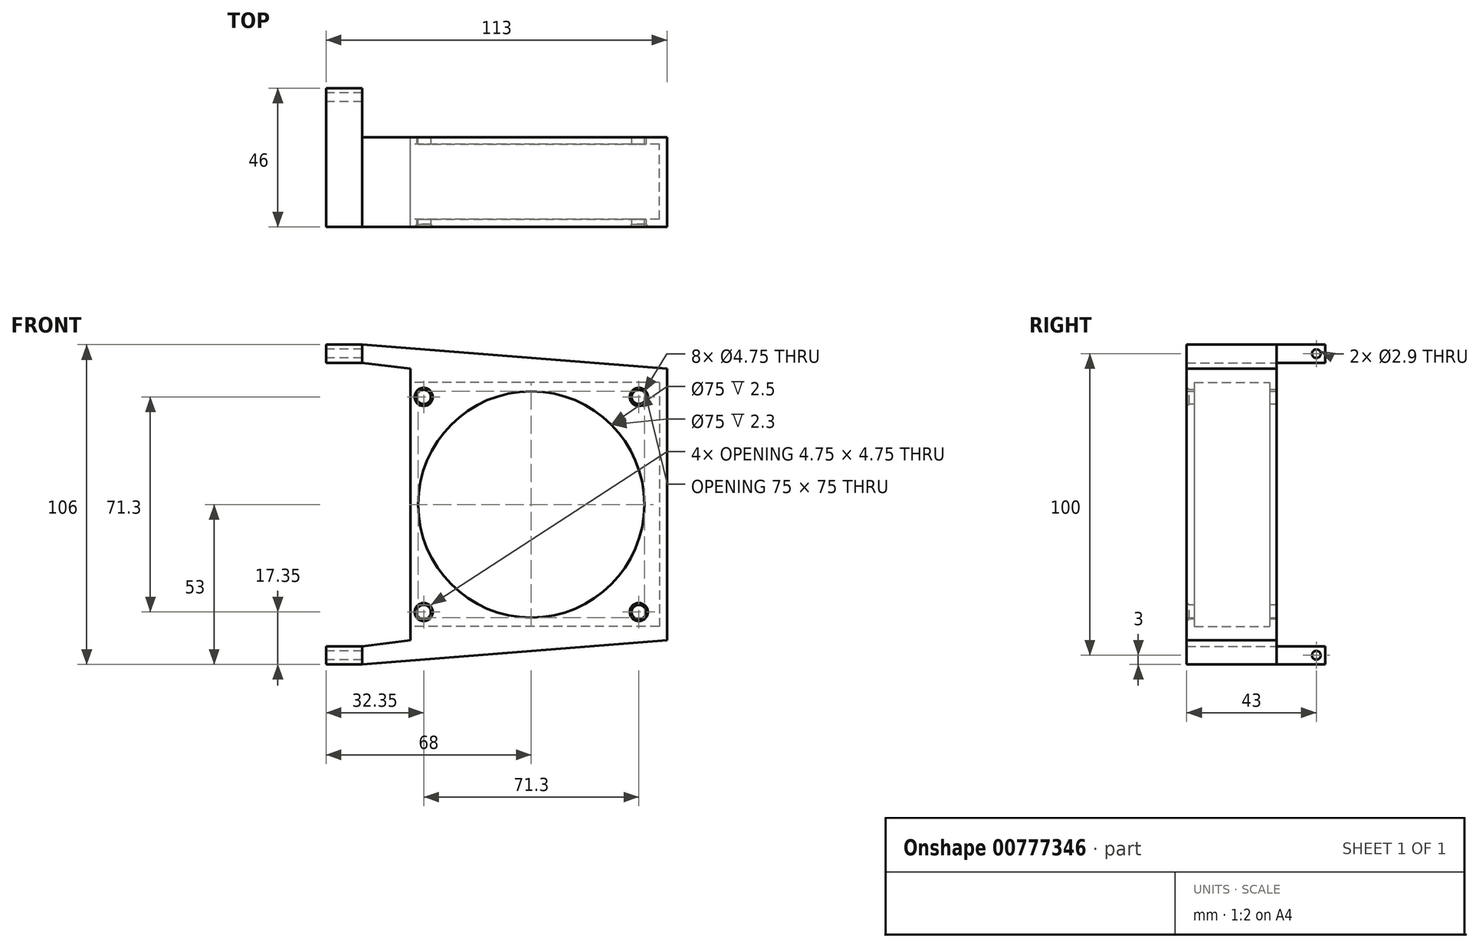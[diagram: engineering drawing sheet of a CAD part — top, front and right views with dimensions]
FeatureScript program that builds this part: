
annotation { "Feature Type Name" : "Feature", "Feature Type Description" : "" }
export const myFeature = defineFeature(function(context is Context, id is Id, definition is map)
    precondition{}
    {
        {
            var Q0;
            Q0=qCreatedBy(makeId("Front.planeOp"),FACE);
            var sketch = newSketch(context, id + "F0", { "sketchPlane" : qUnion([Q0])});
            skLineSegment(sketch, "E0.bottom", {"start": v(-35.65, 35.65) * mm, "end": v(35.65, 35.65) * mm, "construction": true});
            skLineSegment(sketch, "E0.top", {"start": v(-35.65, -35.65) * mm, "end": v(35.65, -35.65) * mm, "construction": true});
            skLineSegment(sketch, "E0.left", {"start": v(-35.65, 35.65) * mm, "end": v(-35.65, -35.65) * mm, "construction": true});
            skLineSegment(sketch, "E0.right", {"start": v(35.65, 35.65) * mm, "end": v(35.65, -35.65) * mm, "construction": true});
            skPoint(sketch, "E0.middle", {"position": v(0, 0) * mm});
            skLineSegment(sketch, "E1.bottom", {"start": v(-40, 40) * mm, "end": v(40, 40) * mm});
            skLineSegment(sketch, "E1.top", {"start": v(-40, -40) * mm, "end": v(40, -40) * mm});
            skLineSegment(sketch, "E1.left", {"start": v(-40, 40) * mm, "end": v(-40, -40) * mm});
            skLineSegment(sketch, "E1.right", {"start": v(40, 40) * mm, "end": v(40, -40) * mm});
            skPoint(sketch, "E2.middle", {"position": v(-58, 0) * mm});
            skPoint(sketch, "E2.middle.positionSnap0", {"position": v(-40, 0) * mm});
            skPoint(sketch, "E2.centerSnap0", {"position": v(-40, 0) * mm});
            skLineSegment(sketch, "E3.bottom", {"start": v(-68, 50) * mm, "end": v(-48, 50) * mm, "construction": true});
            skLineSegment(sketch, "E3.top", {"start": v(-68, -50) * mm, "end": v(-48, -50) * mm, "construction": true});
            skLineSegment(sketch, "E3.left", {"start": v(-68, 50) * mm, "end": v(-68, -50) * mm, "construction": true});
            skLineSegment(sketch, "E3.right", {"start": v(-48, 50) * mm, "end": v(-48, -50) * mm, "construction": true});
            skLineSegment(sketch, "E4.bottom", {"start": v(-56, 47) * mm, "end": v(-68, 47) * mm});
            skLineSegment(sketch, "E4.top", {"start": v(-56, 53) * mm, "end": v(-68, 53) * mm});
            skLineSegment(sketch, "E4.left", {"start": v(-56, 47) * mm, "end": v(-56, 53) * mm});
            skLineSegment(sketch, "E4.right", {"start": v(-68, 47) * mm, "end": v(-68, 53) * mm});
            skPoint(sketch, "E4.middle", {"position": v(-62, 50) * mm});
            skLineSegment(sketch, "E5.MirrorCS", {"start": v(-68, -47) * mm, "end": v(-68, -53) * mm});
            skLineSegment(sketch, "E6.MirrorCS", {"start": v(-56, -47) * mm, "end": v(-68, -47) * mm});
            skLineSegment(sketch, "E7.MirrorCS", {"start": v(-56, -53) * mm, "end": v(-68, -53) * mm});
            skLineSegment(sketch, "E8.MirrorCS", {"start": v(-56, -47) * mm, "end": v(-56, -53) * mm});
            skPoint(sketch, "E9.MirrorP", {"position": v(-62, -50) * mm});
            skLineSegment(sketch, "E10.bottom", {"start": v(-68, 47) * mm, "end": v(-56, 47) * mm});
            skLineSegment(sketch, "E10.top", {"start": v(-68, -47) * mm, "end": v(-56, -47) * mm});
            skLineSegment(sketch, "E10.left", {"start": v(-68, 47) * mm, "end": v(-68, -47) * mm});
            skLineSegment(sketch, "E10.right", {"start": v(-56, 47) * mm, "end": v(-56, -47) * mm});
            skLineSegment(sketch, "E11.bottom", {"start": v(40, 40) * mm, "end": v(45, 40) * mm, "construction": true});
            skLineSegment(sketch, "E11.top", {"start": v(40, 45) * mm, "end": v(45, 45) * mm, "construction": true});
            skLineSegment(sketch, "E11.left", {"start": v(40, 40) * mm, "end": v(40, 45) * mm, "construction": true});
            skLineSegment(sketch, "E11.right", {"start": v(45, 40) * mm, "end": v(45, 45) * mm, "construction": true});
            skLineSegment(sketch, "E12.MirrorCS", {"start": v(45, -40) * mm, "end": v(45, -45) * mm, "construction": true});
            skLineSegment(sketch, "E13.MirrorCS", {"start": v(40, -40) * mm, "end": v(45, -40) * mm, "construction": true});
            skLineSegment(sketch, "E14.MirrorCS", {"start": v(40, -45) * mm, "end": v(45, -45) * mm, "construction": true});
            skLineSegment(sketch, "E15.MirrorCS", {"start": v(40, -40) * mm, "end": v(40, -45) * mm, "construction": true});
            skLineSegment(sketch, "E16.bottom", {"start": v(45, 45) * mm, "end": v(-40, 45) * mm});
            skLineSegment(sketch, "E16.top", {"start": v(45, -45) * mm, "end": v(-40, -45) * mm});
            skLineSegment(sketch, "E16.left", {"start": v(45, 45) * mm, "end": v(45, -45) * mm});
            skLineSegment(sketch, "E16.right", {"start": v(-40, 45) * mm, "end": v(-40, -45) * mm});
            skCircle(sketch, "E17", {"center": v(0, 0) * mm, "radius": 37.5 * mm});
            skLineSegment(sketch, "E18", {"start": v(-56, 53) * mm, "end": v(45, 45) * mm});
            skLineSegment(sketch, "E19", {"start": v(-56, 47) * mm, "end": v(-40, 45) * mm});
            skLineSegment(sketch, "E20.MirrorCS", {"start": v(-56, -53) * mm, "end": v(45, -45) * mm});
            skLineSegment(sketch, "E21.MirrorCS", {"start": v(-56, -47) * mm, "end": v(-40, -45) * mm});
            skLineSegment(sketch, "E22", {"start": v(0, 0) * mm, "end": v(-40, 0) * mm, "construction": true});
            skLineSegment(sketch, "E23", {"start": v(-40, -45) * mm, "end": v(-40, -51.73) * mm, "construction": true});
            skLineSegment(sketch, "E24", {"start": v(-40, 45) * mm, "end": v(-40, 51.73) * mm, "construction": true});
            skSolve(sketch);
        }
        {
            var Q0;
            Q0=makeQuery(id+"F0.imprint","IMPRINT",FACE,{"disambiguationData":[TD([[makeQuery(id+"F0.imprint","IMPRINT",EDGE,{"derivedFrom":sQuery(id+"F0.wireOp",EDGE,"E4.top")}),1.0]])]});
            var Q1;
            Q1=makeQuery(id+"F0.imprint","IMPRINT",FACE,{"disambiguationData":[TD([[makeQuery(id+"F0.imprint","IMPRINT",EDGE,{"derivedFrom":sQuery(id+"F0.wireOp",EDGE,"E5.MirrorCS")}),1.0]])]});
            extrude(context, id + "F1", {"entities" : qUnion([Q0, Q1]), "depth" : 46 * mm, "offsetDistance" : 25 * mm});
        }
        {
            var Q0;
            Q0=makeQuery(id+"F1.opExtrude","SWEPT_FACE",FACE,{"disambiguationData":[OSD([sQuery(id+"F0.wireOp",EDGE,"E4.right")])]});
            var sketch = newSketch(context, id + "F2", { "sketchPlane" : qUnion([Q0])});
            skLineSegment(sketch, "E25", {"start": v(0, 50) * mm, "end": v(3, 50) * mm, "construction": true});
            skSolve(sketch);
        }
        {
            var Q0;
            Q0=sQuery(id+"F2.wireOp",VERTEX,"E25.end");
            var Q1;
            Q1=makeQuery(id+"F1.opExtrude","SWEPT_BODY",BODY,{"disambiguationData":[OSD([sQuery(id+"F0.wireOp",EDGE,"E4.top"),sQuery(id+"F0.wireOp",EDGE,"E4.left"),sQuery(id+"F0.wireOp",EDGE,"E4.right"),sQuery(id+"F0.wireOp",EDGE,"E10.bottom")])]});
            hole(context, id + "F3", {"style" : HoleStyle.SIMPLE, "endStyle" : HoleEndStyle.BLIND, "holeDiameter" : 2.9 * mm, "majorDiameter" : 5 * mm, "holeDepth" : 12 * mm, "isTappedThrough" : true, "tappedDepth" : 12 * mm, "tapClearance" : 3, "locations" : qUnion([Q0]), "scope" : qUnion([Q1])});
        }
        {
            var Q0;
            Q0=makeQuery(id+"F1.opExtrude","SWEPT_FACE",FACE,{"disambiguationData":[OSD([sQuery(id+"F0.wireOp",EDGE,"E5.MirrorCS")])]});
            var sketch = newSketch(context, id + "F4", { "sketchPlane" : qUnion([Q0])});
            skLineSegment(sketch, "E26", {"start": v(0, -50) * mm, "end": v(3, -50) * mm, "construction": true});
            skSolve(sketch);
        }
        {
            var Q0;
            Q0=sQuery(id+"F4.wireOp",VERTEX,"E26.end");
            var Q1;
            Q1=makeQuery(id+"F1.opExtrude","SWEPT_BODY",BODY,{"disambiguationData":[OSD([sQuery(id+"F0.wireOp",EDGE,"E5.MirrorCS"),sQuery(id+"F0.wireOp",EDGE,"E7.MirrorCS"),sQuery(id+"F0.wireOp",EDGE,"E8.MirrorCS"),sQuery(id+"F0.wireOp",EDGE,"E10.top")])]});
            hole(context, id + "F5", {"style" : HoleStyle.SIMPLE, "endStyle" : HoleEndStyle.BLIND, "holeDiameter" : 2.9 * mm, "majorDiameter" : 5 * mm, "holeDepth" : 12 * mm, "isTappedThrough" : true, "tappedDepth" : 12 * mm, "tapClearance" : 3, "locations" : qUnion([Q0]), "scope" : qUnion([Q1])});
        }
        {
            var Q0;
            Q0=makeQuery(id+"F0.imprint","IMPRINT",FACE,{"disambiguationData":[TD([[makeQuery(id+"F0.imprint","IMPRINT",EDGE,{"derivedFrom":sQuery(id+"F0.wireOp",EDGE,"E4.left")}),-1.0]])]});
            var Q1;
            {var subQ2=sQuery(id+"F0.wireOp",EDGE,"E1.bottom");Q1=makeQuery(id+"F0.imprint","IMPRINT",FACE,{"disambiguationData":[TD([[makeQuery(id+"F0.imprint","IMPRINT",EDGE,{"derivedFrom":subQ2}),1.0]])]});}
            var Q2;
            {var subQ1=sQuery(id+"F0.wireOp",EDGE,"E1.bottom");Q2=makeQuery(id+"F0.imprint","IMPRINT",FACE,{"disambiguationData":[TD([[makeQuery(id+"F0.imprint","IMPRINT",EDGE,{"derivedFrom":subQ1}),-1.0]])]});}
            var Q3;
            Q3=makeQuery(id+"F0.imprint","IMPRINT",FACE,{"disambiguationData":[TD([[makeQuery(id+"F0.imprint","IMPRINT",EDGE,{"derivedFrom":sQuery(id+"F0.wireOp",EDGE,"E8.MirrorCS")}),1.0]])]});
            extrude(context, id + "F6", {"entities" : qUnion([Q0, Q1, Q2, Q3]), "depth" : 46 * mm, "offsetDistance" : 25 * mm, "hasSecondDirection" : true, "secondDirectionOppositeDirection" : true, "secondDirectionDepth" : -16.2 * mm});
        }
        {
            var Q0;
            Q0=makeQuery(id+"F6.opExtrude","SWEPT_FACE",FACE,{"disambiguationData":[OSD([sQuery(id+"F0.wireOp",EDGE,"E16.right")])]});
            var sketch = newSketch(context, id + "F7", { "sketchPlane" : qUnion([Q0])});
            skLineSegment(sketch, "E27.bottom", {"start": v(46, 45) * mm, "end": v(43.5, 45) * mm, "construction": true});
            skLineSegment(sketch, "E27.top", {"start": v(46, -45) * mm, "end": v(43.5, -45) * mm, "construction": true});
            skLineSegment(sketch, "E27.left", {"start": v(46, 45) * mm, "end": v(46, -45) * mm, "construction": true});
            skLineSegment(sketch, "E27.right", {"start": v(43.5, 45) * mm, "end": v(43.5, -45) * mm, "construction": true});
            skLineSegment(sketch, "E28", {"start": v(43.5, 0) * mm, "end": v(43.5, 40.5) * mm, "construction": true});
            skLineSegment(sketch, "E29", {"start": v(43.5, 40.5) * mm, "end": v(43.5, 0) * mm, "construction": true});
            skLineSegment(sketch, "E30", {"start": v(43.5, 0) * mm, "end": v(43.5, -40.5) * mm, "construction": true});
            skLineSegment(sketch, "E31.bottom", {"start": v(43.5, 40.5) * mm, "end": v(18.5, 40.5) * mm});
            skLineSegment(sketch, "E31.top", {"start": v(43.5, -40.5) * mm, "end": v(18.5, -40.5) * mm});
            skLineSegment(sketch, "E31.left", {"start": v(43.5, 40.5) * mm, "end": v(43.5, -40.5) * mm});
            skLineSegment(sketch, "E31.right", {"start": v(18.5, 40.5) * mm, "end": v(18.5, -40.5) * mm});
            skSolve(sketch);
        }
        {
            var Q0;
            Q0=makeQuery(id+"F7.imprint","IMPRINT",FACE,{"disambiguationData":[TD([[makeQuery(id+"F7.imprint","IMPRINT",EDGE,{"derivedFrom":sQuery(id+"F7.wireOp",EDGE,"E31.bottom")}),1.0]])]});
            extrude(context, id + "F8", {"entities" : qUnion([Q0]), "operationType" : NewBodyOperationType.REMOVE, "oppositeDirection" : true, "depth" : 82.5 * mm, "offsetDistance" : 25 * mm});
        }
        {
            var Q0;
            Q0=makeQuery(id+"F6.opExtrude","CAP_FACE",FACE,{"disambiguationData":[OSD([sQuery(id+"F0.wireOp",EDGE,"E4.left"),sQuery(id+"F0.wireOp",EDGE,"E8.MirrorCS"),sQuery(id+"F0.wireOp",EDGE,"E16.left"),sQuery(id+"F0.wireOp",EDGE,"E16.right"),sQuery(id+"F0.wireOp",EDGE,"E17"),sQuery(id+"F0.wireOp",EDGE,"E18"),sQuery(id+"F0.wireOp",EDGE,"E19"),sQuery(id+"F0.wireOp",EDGE,"E20.MirrorCS"),sQuery(id+"F0.wireOp",EDGE,"E21.MirrorCS")])],"isStart":false});
            var sketch = newSketch(context, id + "F9", { "sketchPlane" : qUnion([Q0])});
            skLineSegment(sketch, "E32.bottom", {"start": v(-35.65, 35.65) * mm, "end": v(35.65, 35.65) * mm, "construction": true});
            skLineSegment(sketch, "E32.top", {"start": v(-35.65, -35.65) * mm, "end": v(35.65, -35.65) * mm, "construction": true});
            skLineSegment(sketch, "E32.left", {"start": v(-35.65, 35.65) * mm, "end": v(-35.65, -35.65) * mm, "construction": true});
            skLineSegment(sketch, "E32.right", {"start": v(35.65, 35.65) * mm, "end": v(35.65, -35.65) * mm, "construction": true});
            skPoint(sketch, "E32.middle", {"position": v(0, 0) * mm});
            skSolve(sketch);
        }
        {
            var Q0;
            Q0=sQuery(id+"F9.wireOp",VERTEX,"E32.bottom.end");
            var Q1;
            Q1=sQuery(id+"F9.wireOp",VERTEX,"E32.top.end");
            var Q2;
            Q2=sQuery(id+"F9.wireOp",VERTEX,"E32.top.start");
            var Q3;
            Q3=sQuery(id+"F9.wireOp",VERTEX,"E32.bottom.start");
            var Q4;
            Q4=makeQuery(id+"F6.opExtrude","SWEPT_BODY",BODY,{"disambiguationData":[OSD([sQuery(id+"F0.wireOp",EDGE,"E4.left"),sQuery(id+"F0.wireOp",EDGE,"E8.MirrorCS"),sQuery(id+"F0.wireOp",EDGE,"E16.left"),sQuery(id+"F0.wireOp",EDGE,"E16.right"),sQuery(id+"F0.wireOp",EDGE,"E17"),sQuery(id+"F0.wireOp",EDGE,"E18"),sQuery(id+"F0.wireOp",EDGE,"E19"),sQuery(id+"F0.wireOp",EDGE,"E20.MirrorCS"),sQuery(id+"F0.wireOp",EDGE,"E21.MirrorCS")])]});
            hole(context, id + "F10", {"style" : HoleStyle.C_SINK, "endStyle" : HoleEndStyle.BLIND, "holeDiameter" : 4.75 * mm, "cSinkDiameter" : 6 * mm, "cSinkAngle" : 70 * degree, "majorDiameter" : 5 * mm, "holeDepth" : 30 * mm, "isTappedThrough" : true, "tappedDepth" : 12 * mm, "tapClearance" : 3, "locations" : qUnion([Q0, Q1, Q2, Q3]), "scope" : qUnion([Q4])});
        }
    });
